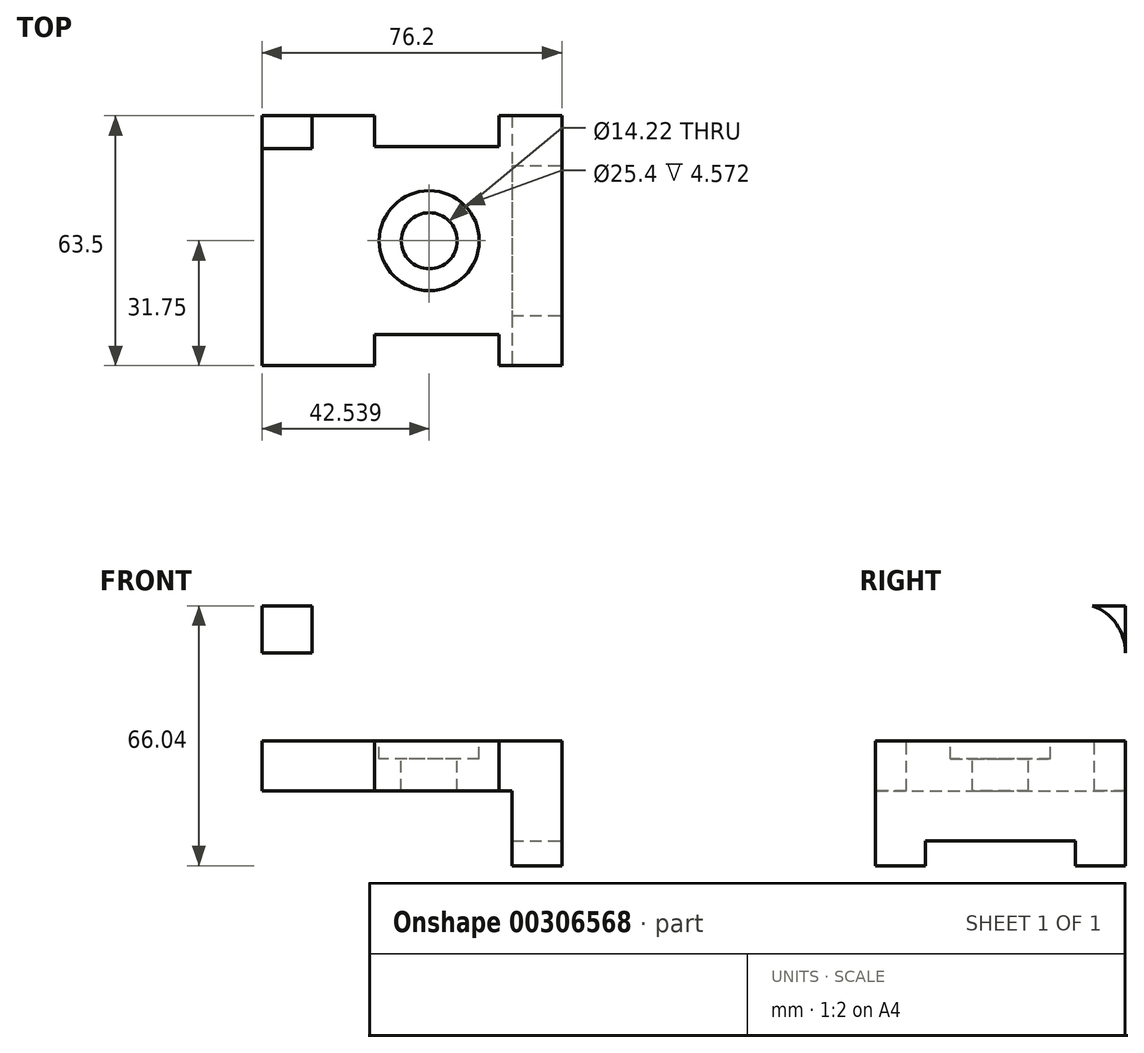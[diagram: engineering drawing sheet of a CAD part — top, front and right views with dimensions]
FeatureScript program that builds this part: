
annotation { "Feature Type Name" : "Feature", "Feature Type Description" : "" }
export const myFeature = defineFeature(function(context is Context, id is Id, definition is map)
    precondition{}
    {
        {
            var Q0;
            Q0=qCreatedBy(makeId("Front.planeOp"),FACE);
            var sketch = newSketch(context, id + "F0", { "sketchPlane" : qUnion([Q0])});
            skLineSegment(sketch, "E0", {"start": v(0, 0) * mm, "end": v(60.2, 0) * mm});
            skLineSegment(sketch, "E1", {"start": v(60.2, 0) * mm, "end": v(60.2, -19.05) * mm});
            skLineSegment(sketch, "E2", {"start": v(60.2, -19.05) * mm, "end": v(76.2, -19.05) * mm});
            skLineSegment(sketch, "E3", {"start": v(76.2, -19.05) * mm, "end": v(76.2, 12.7) * mm});
            skLineSegment(sketch, "E4", {"start": v(76.2, 12.7) * mm, "end": v(12.7, 12.7) * mm});
            skLineSegment(sketch, "E5", {"start": v(12.7, 12.7) * mm, "end": v(12.7, 47) * mm});
            skLineSegment(sketch, "E6", {"start": v(12.7, 47) * mm, "end": v(0, 47) * mm});
            skLineSegment(sketch, "E7", {"start": v(0, 47) * mm, "end": v(0, 0) * mm});
            skSolve(sketch);
        }
        {
            var Q0;
            Q0 = qSketchRegion(id + "F0", true);
            extrude(context, id + "F1", {"entities" : qUnion([Q0]), "endBound" : BoundingType.SYMMETRIC, "depth" : 63.5 * mm});
        }
        {
            var Q0;
            Q0=makeQuery(id+"F1.opExtrude","SWEPT_FACE",FACE,{"disambiguationData":[OSD([sQuery(id+"F0.wireOp",EDGE,"E4")])]});
            var sketch = newSketch(context, id + "F2", { "sketchPlane" : qUnion([Q0])});
            skLineSegment(sketch, "E8", {"start": v(12.7, 31.75) * mm, "end": v(28.7, 31.75) * mm});
            skLineSegment(sketch, "E9", {"start": v(28.7, 31.75) * mm, "end": v(28.7, 23.88) * mm});
            skLineSegment(sketch, "E10", {"start": v(28.7, 23.88) * mm, "end": v(60.2, 23.88) * mm});
            skLineSegment(sketch, "E11", {"start": v(60.2, 23.88) * mm, "end": v(60.2, 31.75) * mm});
            skLineSegment(sketch, "E12", {"start": v(60.2, 31.75) * mm, "end": v(76.2, 31.75) * mm});
            skLineSegment(sketch, "E13", {"start": v(76.2, 31.75) * mm, "end": v(76.2, -31.75) * mm});
            skLineSegment(sketch, "E14", {"start": v(76.2, -31.75) * mm, "end": v(60.2, -31.75) * mm});
            skLineSegment(sketch, "E15", {"start": v(60.2, -31.75) * mm, "end": v(60.2, -23.88) * mm});
            skLineSegment(sketch, "E16", {"start": v(60.2, -23.88) * mm, "end": v(28.7, -23.88) * mm});
            skLineSegment(sketch, "E17", {"start": v(28.7, -23.88) * mm, "end": v(28.7, -31.75) * mm});
            skLineSegment(sketch, "E18", {"start": v(28.7, -31.75) * mm, "end": v(12.7, -31.75) * mm});
            skLineSegment(sketch, "E19", {"start": v(12.7, -31.75) * mm, "end": v(12.7, 31.75) * mm});
            skSolve(sketch);
        }
        {
            var Q0;
            {var subQ0=sQuery(id+"F2.wireOp",EDGE,"E9");Q0=makeQuery(id+"F2.imprint","IMPRINT",FACE,{"disambiguationData":[TD([[makeQuery(id+"F2.imprint","IMPRINT",EDGE,{"derivedFrom":subQ0}),1.0]])]});}
            var Q1;
            {var subQ0=sQuery(id+"F2.wireOp",EDGE,"E15");Q1=makeQuery(id+"F2.imprint","IMPRINT",FACE,{"disambiguationData":[TD([[makeQuery(id+"F2.imprint","IMPRINT",EDGE,{"derivedFrom":subQ0}),1.0]])]});}
            extrude(context, id + "F3", {"entities" : qUnion([Q0, Q1]), "operationType" : NewBodyOperationType.REMOVE, "endBound" : BoundingType.THROUGH_ALL, "oppositeDirection" : true, "depth" : 25.4 * mm});
        }
        {
            var Q0;
            Q0=makeQuery(id+"F1.opExtrude","SWEPT_FACE",FACE,{"disambiguationData":[OSD([sQuery(id+"F0.wireOp",EDGE,"E4")])]});
            var sketch = newSketch(context, id + "F4", { "sketchPlane" : qUnion([Q0])});
            skCircle(sketch, "E20", {"center": v(42.54, 0) * mm, "radius": 7.11 * mm});
            skSolve(sketch);
        }
        {
            var Q0;
            Q0 = qSketchRegion(id + "F4", true);
            extrude(context, id + "F5", {"entities" : qUnion([Q0]), "operationType" : NewBodyOperationType.REMOVE, "endBound" : BoundingType.THROUGH_ALL, "oppositeDirection" : true, "depth" : 25.4 * mm});
        }
        {
            var Q0;
            Q0=makeQuery(id+"F1.opExtrude","SWEPT_FACE",FACE,{"disambiguationData":[OSD([sQuery(id+"F0.wireOp",EDGE,"E4")])]});
            var sketch = newSketch(context, id + "F6", { "sketchPlane" : qUnion([Q0])});
            skCircle(sketch, "E21", {"center": v(42.54, 0) * mm, "radius": 12.7 * mm});
            skSolve(sketch);
        }
        {
            var Q0;
            Q0 = qSketchRegion(id + "F6", true);
            extrude(context, id + "F7", {"entities" : qUnion([Q0]), "operationType" : NewBodyOperationType.REMOVE, "oppositeDirection" : true, "depth" : 4.57 * mm});
        }
        {
            var Q0;
            Q0=makeQuery(id+"F1.opExtrude","SWEPT_FACE",FACE,{"disambiguationData":[OSD([sQuery(id+"F0.wireOp",EDGE,"E3")])]});
            var sketch = newSketch(context, id + "F8", { "sketchPlane" : qUnion([Q0])});
            skLineSegment(sketch, "E22", {"start": v(-19.05, -19.05) * mm, "end": v(-19.05, -12.7) * mm});
            skLineSegment(sketch, "E23", {"start": v(-19.05, -12.7) * mm, "end": v(19.05, -12.7) * mm});
            skLineSegment(sketch, "E24", {"start": v(19.05, -12.7) * mm, "end": v(19.05, -19.05) * mm});
            skLineSegment(sketch, "E25", {"start": v(19.05, -19.05) * mm, "end": v(-19.05, -19.05) * mm});
            skSolve(sketch);
        }
        {
            var Q0;
            Q0 = qSketchRegion(id + "F8", true);
            extrude(context, id + "F9", {"entities" : qUnion([Q0]), "operationType" : NewBodyOperationType.REMOVE, "endBound" : BoundingType.THROUGH_ALL, "oppositeDirection" : true, "depth" : 25.4 * mm});
        }
        {
            var Q0;
            {var subQ0=sQuery(id+"F0.wireOp",EDGE,"E4");var subQ1=sQuery(id+"F0.wireOp",EDGE,"E3");var subQ2=sQuery(id+"F0.wireOp",EDGE,"E2");var subQ3=sQuery(id+"F0.wireOp",EDGE,"E1");Q0=makeQuery(id+"F3.boolean.opBoolean","SPLIT",FACE,{"disambiguationData":[TD([makeQuery(id+"F1.opExtrude","SWEPT_FACE",FACE,{"disambiguationData":[OSD([subQ3])]})])],"derivedFrom":makeQuery(id+"F1.opExtrude","CAP_FACE",FACE,{"disambiguationData":[OSD([sQuery(id+"F0.wireOp",EDGE,"E0"),subQ3,subQ2,subQ1,subQ0,sQuery(id+"F0.wireOp",EDGE,"E5"),sQuery(id+"F0.wireOp",EDGE,"E6"),sQuery(id+"F0.wireOp",EDGE,"E7")])],"isStart":false})});}
            var sketch = newSketch(context, id + "F10", { "sketchPlane" : qUnion([Q0])});
            skLineSegment(sketch, "E26", {"start": v(60.2, -19.05) * mm, "end": v(63.5, -19.05) * mm});
            skLineSegment(sketch, "E27", {"start": v(63.5, -19.05) * mm, "end": v(63.5, 0) * mm});
            skLineSegment(sketch, "E28", {"start": v(63.5, 0) * mm, "end": v(60.2, 0) * mm});
            skLineSegment(sketch, "E29", {"start": v(60.2, 0) * mm, "end": v(60.2, -19.05) * mm});
            skSolve(sketch);
        }
        {
            var Q0;
            Q0 = qSketchRegion(id + "F10", true);
            extrude(context, id + "F11", {"entities" : qUnion([Q0]), "operationType" : NewBodyOperationType.REMOVE, "endBound" : BoundingType.THROUGH_ALL, "oppositeDirection" : true, "depth" : 25.4 * mm});
        }
        {
            var Q0;
            Q0=makeQuery(id+"F1.opExtrude","SWEPT_FACE",FACE,{"disambiguationData":[OSD([sQuery(id+"F0.wireOp",EDGE,"E5")])]});
            var sketch = newSketch(context, id + "F12", { "sketchPlane" : qUnion([Q0])});
            skArc(sketch, "E30", {"start": v(-23.38, 46.99) * mm, "mid": v(-29.45, 42.34) * mm, "end": v(-31.75, 35.05) * mm});
            skLineSegment(sketch, "E31", {"start": v(0, 57.99) * mm, "end": v(0, 15.1) * mm, "construction": true});
            skPoint(sketch, "E31.endSnap0", {"position": v(0, 12.7) * mm});
            skArc(sketch, "E32.MirrorCS", {"start": v(23.38, 47) * mm, "mid": v(29.45, 42.34) * mm, "end": v(31.75, 35.05) * mm});
            skCircle(sketch, "E33", {"center": v(-19.05, 35.05) * mm, "radius": 3.94 * mm});
            skCircle(sketch, "E34", {"center": v(19.05, 35.05) * mm, "radius": 3.94 * mm});
            skLineSegment(sketch, "E35", {"start": v(-19.05, 38.99) * mm, "end": v(19.05, 38.99) * mm});
            skLineSegment(sketch, "E36", {"start": v(-19.05, 31.12) * mm, "end": v(19.05, 31.12) * mm});
            skSolve(sketch);
        }
        {
            var Q0;
            {var subQ0=sQuery(id+"F12.wireOp",EDGE,"E30");Q0=makeQuery(id+"F12.imprint","IMPRINT",FACE,{"disambiguationData":[TD([[makeQuery(id+"F12.imprint","IMPRINT",EDGE,{"derivedFrom":subQ0}),-1.0]])]});}
            var Q1;
            {var subQ0=sQuery(id+"F12.wireOp",EDGE,"E32.MirrorCS");Q1=makeQuery(id+"F12.imprint","IMPRINT",FACE,{"disambiguationData":[TD([[makeQuery(id+"F12.imprint","IMPRINT",EDGE,{"derivedFrom":subQ0}),1.0]])]});}
            extrude(context, id + "F13", {"entities" : qUnion([Q0, Q1]), "operationType" : NewBodyOperationType.REMOVE, "endBound" : BoundingType.THROUGH_ALL, "oppositeDirection" : true, "depth" : 25.4 * mm});
        }
        {
            var Q0;
            Q0 = qSketchRegion(id + "F12", true);
            extrude(context, id + "F14", {"entities" : qUnion([Q0]), "operationType" : NewBodyOperationType.REMOVE, "endBound" : BoundingType.THROUGH_ALL, "oppositeDirection" : true, "depth" : 25.4 * mm});
        }
    });
